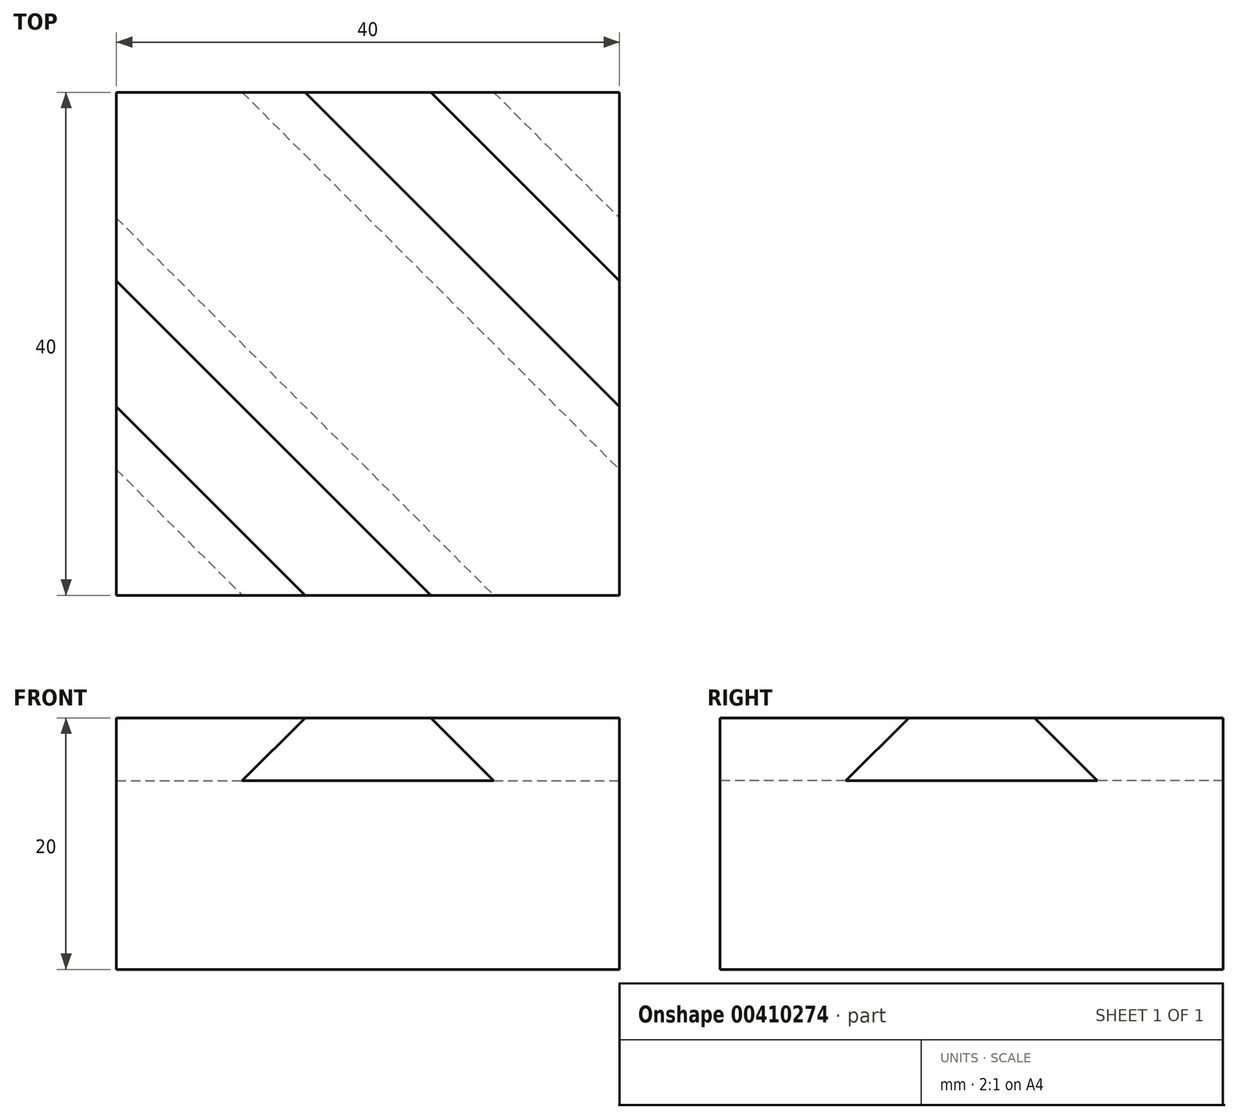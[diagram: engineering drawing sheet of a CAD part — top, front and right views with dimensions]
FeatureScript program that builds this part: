
annotation { "Feature Type Name" : "Feature", "Feature Type Description" : "" }
export const myFeature = defineFeature(function(context is Context, id is Id, definition is map)
    precondition{}
    {
        {
            var Q0;
            Q0=qCreatedBy(makeId("Top.planeOp"),FACE);
            var sketch = newSketch(context, id + "F0", { "sketchPlane" : qUnion([Q0])});
            skLineSegment(sketch, "E0.bottom", {"start": v(-20, 20) * mm, "end": v(20, 20) * mm});
            skLineSegment(sketch, "E0.top", {"start": v(-20, -20) * mm, "end": v(20, -20) * mm});
            skLineSegment(sketch, "E0.left", {"start": v(-20, 20) * mm, "end": v(-20, -20) * mm});
            skLineSegment(sketch, "E0.right", {"start": v(20, 20) * mm, "end": v(20, -20) * mm});
            skSolve(sketch);
        }
        {
            var Q0;
            Q0=makeQuery(id+"F0.imprint","IMPRINT",FACE,{"disambiguationData":[TD([[makeQuery(id+"F0.imprint","IMPRINT",EDGE,{"derivedFrom":sQuery(id+"F0.wireOp",EDGE,"E0.bottom")}),-1.0]])]});
            extrude(context, id + "F1", {"entities" : qUnion([Q0]), "depth" : 40 * mm});
        }
        {
            var Q0;
            Q0=makeQuery(id+"F1.opExtrude","CAP_VERTEX",VERTEX,{"disambiguationData":[OSD([sQuery(id+"F0.wireOp",EDGE,"E0.top"),sQuery(id+"F0.wireOp",EDGE,"E0.left")])],"isStart":false});
            var Q1;
            Q1=makeQuery(id+"F1.opExtrude","CAP_VERTEX",VERTEX,{"disambiguationData":[OSD([sQuery(id+"F0.wireOp",EDGE,"E0.bottom"),sQuery(id+"F0.wireOp",EDGE,"E0.right")])],"isStart":false});
            var Q2;
            Q2=makeQuery(id+"F1.opExtrude","CAP_VERTEX",VERTEX,{"disambiguationData":[OSD([sQuery(id+"F0.wireOp",EDGE,"E0.top"),sQuery(id+"F0.wireOp",EDGE,"E0.left")])],"isStart":true});
            cPlane(context, id + "F2", {"entities" : qUnion([Q0, Q1, Q2]), "cplaneType" : CPlaneType.THREE_POINT, "offset" : 25 * mm, "width" : 150 * mm, "height" : 150 * mm});
        }
        {
            var Q0;
            Q0=qCreatedBy(id+"F2.planeOp",FACE);
            var sketch = newSketch(context, id + "F3", { "sketchPlane" : qUnion([Q0])});
            skLineSegment(sketch, "E1", {"start": v(-39.17, 20) * mm, "end": v(45.98, 20) * mm, "construction": true});
            skLineSegment(sketch, "E2", {"start": v(0, 0) * mm, "end": v(0, 50.55) * mm, "construction": true});
            skLineSegment(sketch, "E3", {"start": v(-28.28, 30) * mm, "end": v(0, 30) * mm, "construction": true});
            skLineSegment(sketch, "E4", {"start": v(-7.07, 56.47) * mm, "end": v(-7.07, -12.7) * mm, "construction": true});
            skLineSegment(sketch, "E5", {"start": v(7.07, 43.37) * mm, "end": v(7.07, -11.1) * mm, "construction": true});
            skLineSegment(sketch, "E6", {"start": v(10.6, 56.47) * mm, "end": v(10.6, -13.34) * mm, "construction": true});
            skLineSegment(sketch, "E7", {"start": v(-10.6, 44.33) * mm, "end": v(-10.6, -17.65) * mm, "construction": true});
            skLineSegment(sketch, "E8", {"start": v(17.68, 53.44) * mm, "end": v(17.68, -14.62) * mm, "construction": true});
            skLineSegment(sketch, "E9", {"start": v(21.21, 53.12) * mm, "end": v(21.21, -13.5) * mm, "construction": true});
            skLineSegment(sketch, "E10", {"start": v(-21.21, 51.84) * mm, "end": v(-21.21, -14.14) * mm, "construction": true});
            skLineSegment(sketch, "E11", {"start": v(-17.68, 51.52) * mm, "end": v(-17.68, -13.34) * mm, "construction": true});
            skLineSegment(sketch, "E12", {"start": v(-32.7, 15) * mm, "end": v(33.7, 15) * mm, "construction": true});
            skPoint(sketch, "E12.startSnap0", {"position": v(-28.28, 15) * mm});
            skLineSegment(sketch, "E13", {"start": v(-28.28, 20) * mm, "end": v(-17.68, 20) * mm});
            skLineSegment(sketch, "E14", {"start": v(-17.68, 20) * mm, "end": v(-21.21, 15) * mm});
            skLineSegment(sketch, "E15", {"start": v(-21.21, 15) * mm, "end": v(-7.07, 15) * mm});
            skLineSegment(sketch, "E16", {"start": v(-7.07, 15) * mm, "end": v(-10.6, 20) * mm});
            skLineSegment(sketch, "E17", {"start": v(-10.6, 20) * mm, "end": v(10.6, 20) * mm});
            skLineSegment(sketch, "E18", {"start": v(10.6, 20) * mm, "end": v(7.07, 15) * mm});
            skLineSegment(sketch, "E19", {"start": v(7.07, 15) * mm, "end": v(21.21, 15) * mm});
            skLineSegment(sketch, "E20", {"start": v(21.21, 15) * mm, "end": v(17.68, 20) * mm});
            skLineSegment(sketch, "E21", {"start": v(17.68, 20) * mm, "end": v(28.28, 20) * mm});
            skLineSegment(sketch, "E22", {"start": v(-32.54, 40) * mm, "end": v(37.87, 40) * mm, "construction": true});
            skLineSegment(sketch, "E23", {"start": v(-28.28, 20) * mm, "end": v(-28.28, 40) * mm});
            skLineSegment(sketch, "E24", {"start": v(-28.28, 40) * mm, "end": v(28.28, 40) * mm});
            skLineSegment(sketch, "E25", {"start": v(28.28, 40) * mm, "end": v(28.28, 20) * mm});
            skSolve(sketch);
        }
        {
            var Q0;
            Q0 = qSketchRegion(id + "F3", true);
            extrude(context, id + "F4", {"entities" : qUnion([Q0]), "operationType" : NewBodyOperationType.REMOVE, "endBound" : BoundingType.SYMMETRIC, "oppositeDirection" : true, "depth" : 60 * mm});
        }
    });
